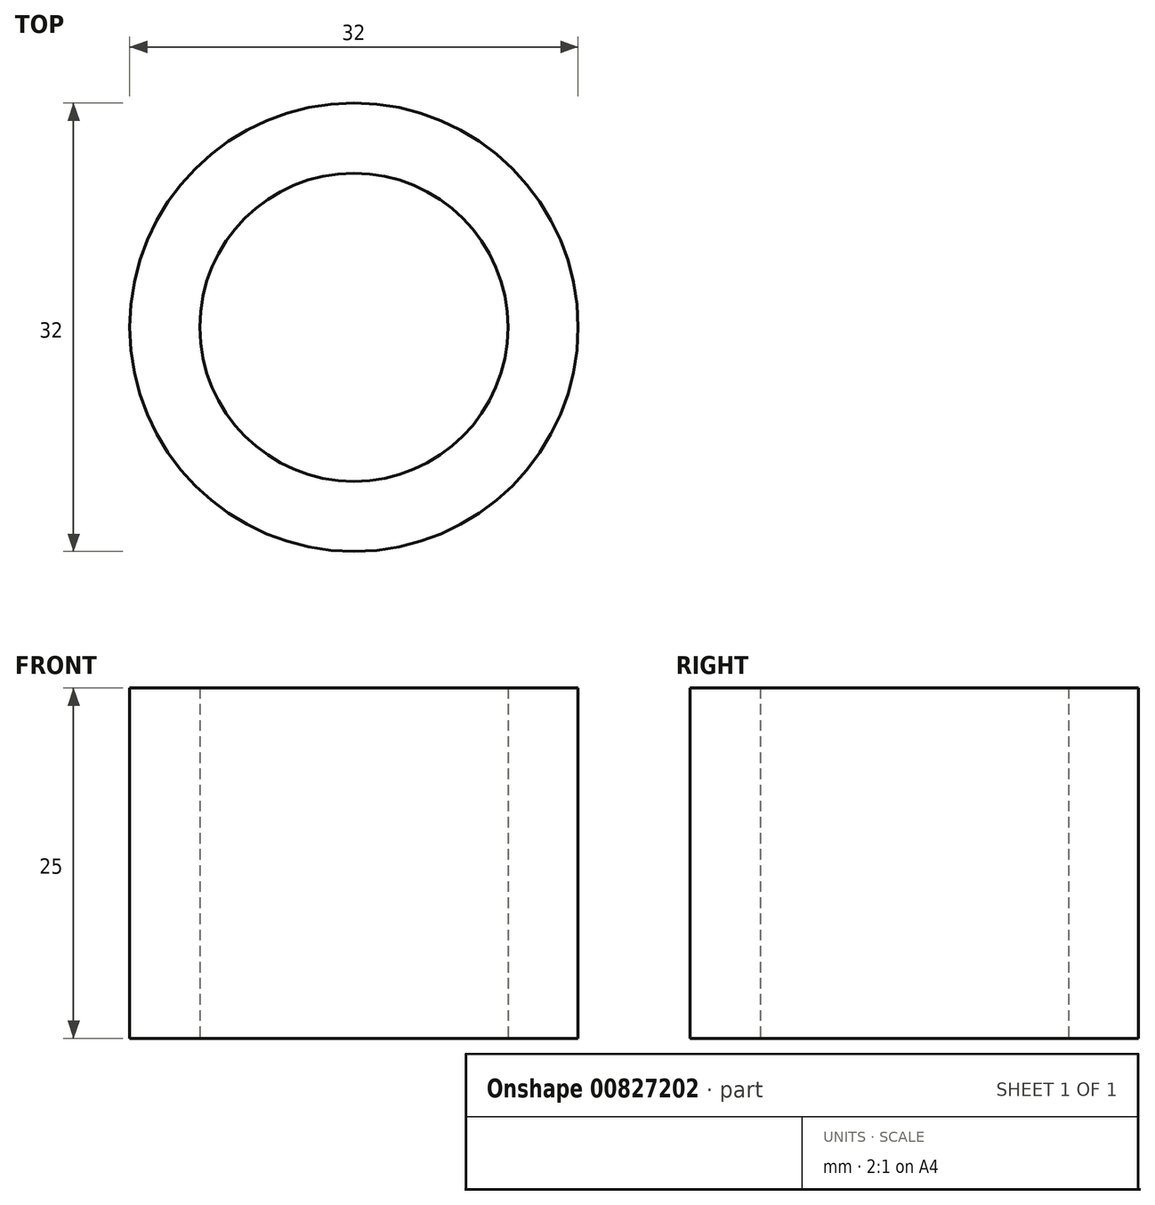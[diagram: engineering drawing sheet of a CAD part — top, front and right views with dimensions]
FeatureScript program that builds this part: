
annotation { "Feature Type Name" : "Feature", "Feature Type Description" : "" }
export const myFeature = defineFeature(function(context is Context, id is Id, definition is map)
    precondition{}
    {
        {
            var Q0;
            Q0=qCreatedBy(makeId("Top.planeOp"),FACE);
            var sketch = newSketch(context, id + "F0", { "sketchPlane" : qUnion([Q0])});
            skCircle(sketch, "E0", {"center": v(0, 0) * mm, "radius": 11 * mm});
            skCircle(sketch, "E1", {"center": v(0, 0) * mm, "radius": 16 * mm});
            skSolve(sketch);
        }
        {
            var Q0;
            Q0 = qSketchRegion(id + "F0", true);
            extrude(context, id + "F1", {"entities" : qUnion([Q0]), "depth" : 25 * mm, "offsetDistance" : 25 * mm});
        }
    });
